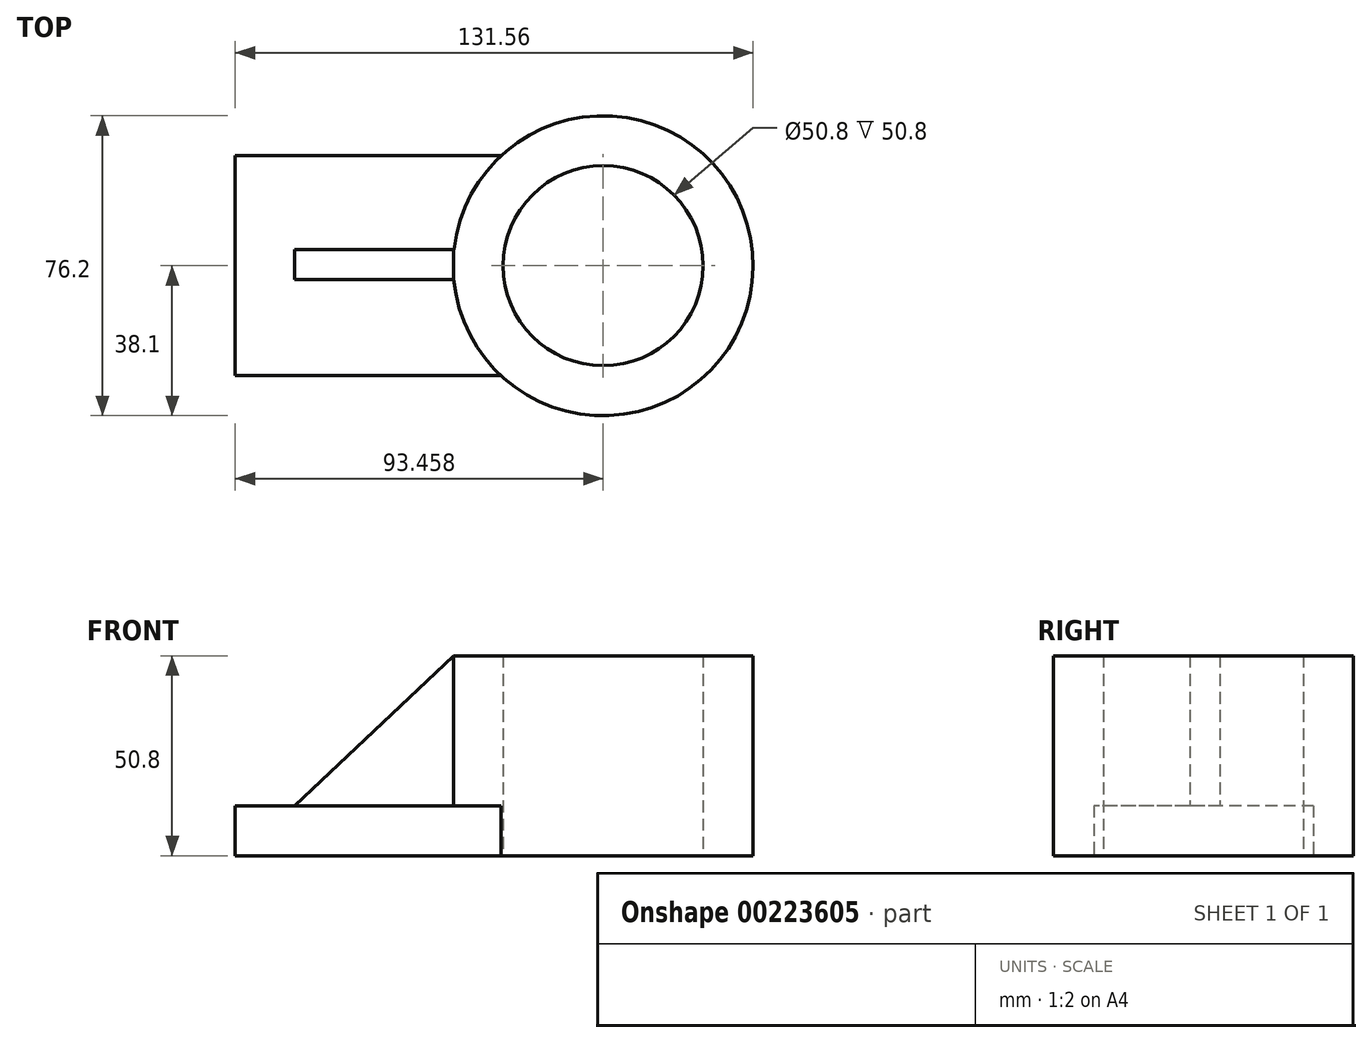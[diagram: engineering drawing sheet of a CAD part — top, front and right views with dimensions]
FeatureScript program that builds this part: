
annotation { "Feature Type Name" : "Feature", "Feature Type Description" : "" }
export const myFeature = defineFeature(function(context is Context, id is Id, definition is map)
    precondition{}
    {
        {
            var Q0;
            Q0=qCreatedBy(makeId("Top.planeOp"),FACE);
            var sketch = newSketch(context, id + "F0", { "sketchPlane" : qUnion([Q0])});
            skCircle(sketch, "E0", {"center": v(38.03, 0) * mm, "radius": 38.1 * mm});
            skCircle(sketch, "E1", {"center": v(38.03, 0) * mm, "radius": 25.4 * mm});
            skSolve(sketch);
        }
        {
            var Q0;
            Q0=makeQuery(id+"F0.imprint","IMPRINT",FACE,{"disambiguationData":[TD([[makeQuery(id+"F0.imprint","IMPRINT",EDGE,{"derivedFrom":sQuery(id+"F0.wireOp",EDGE,"E0")}),1.0]])]});
            extrude(context, id + "F1", {"entities" : qUnion([Q0]), "depth" : 50.8 * mm});
        }
        {
            var Q0;
            Q0=qCreatedBy(makeId("Top.planeOp"),FACE);
            var sketch = newSketch(context, id + "F2", { "sketchPlane" : qUnion([Q0])});
            skLineSegment(sketch, "E2.bottom", {"start": v(12.24, 27.93) * mm, "end": v(-55.43, 27.93) * mm});
            skLineSegment(sketch, "E2.top", {"start": v(12.24, -27.87) * mm, "end": v(-55.43, -27.87) * mm});
            skLineSegment(sketch, "E2.left", {"start": v(12.24, 27.93) * mm, "end": v(12.24, -27.87) * mm});
            skLineSegment(sketch, "E2.right", {"start": v(-55.43, 27.93) * mm, "end": v(-55.43, -27.87) * mm});
            skSolve(sketch);
        }
        {
            var Q0;
            Q0=makeQuery(id+"F2.imprint","IMPRINT",FACE,{"disambiguationData":[TD([[makeQuery(id+"F2.imprint","IMPRINT",EDGE,{"derivedFrom":sQuery(id+"F2.wireOp",EDGE,"E2.bottom")}),1.0]])]});
            extrude(context, id + "F3", {"entities" : qUnion([Q0]), "operationType" : NewBodyOperationType.ADD, "depth" : 12.7 * mm});
        }
        {
            var Q0;
            Q0=makeQuery(id+"F3.opExtrude","CAP_FACE",FACE,{"disambiguationData":[OSD([sQuery(id+"F2.wireOp",EDGE,"E2.bottom"),sQuery(id+"F2.wireOp",EDGE,"E2.top"),sQuery(id+"F2.wireOp",EDGE,"E2.left"),sQuery(id+"F2.wireOp",EDGE,"E2.right")])],"isStart":false});
            var sketch = newSketch(context, id + "F4", { "sketchPlane" : qUnion([Q0])});
            skLineSegment(sketch, "E3.bottom", {"start": v(0.16, 4.17) * mm, "end": v(-40.37, 4.17) * mm});
            skLineSegment(sketch, "E3.top", {"start": v(0.16, -3.45) * mm, "end": v(-40.37, -3.45) * mm});
            skLineSegment(sketch, "E3.left", {"start": v(0.16, 4.17) * mm, "end": v(0.16, -3.45) * mm});
            skLineSegment(sketch, "E3.right", {"start": v(-40.37, 4.17) * mm, "end": v(-40.37, -3.45) * mm});
            skSolve(sketch);
        }
        {
            var Q0;
            {var subQ0=sQuery(id+"F4.wireOp",EDGE,"E3.bottom");Q0=makeQuery(id+"F4.imprint","IMPRINT",FACE,{"disambiguationData":[TD([[makeQuery(id+"F4.imprint","IMPRINT",EDGE,{"derivedFrom":subQ0}),1.0]])]});}
            extrude(context, id + "F5", {"entities" : qUnion([Q0]), "operationType" : NewBodyOperationType.ADD, "depth" : 38.1 * mm});
        }
        {
            var Q0;
            Q0=makeQuery(id+"F5.opExtrude","SWEPT_FACE",FACE,{"disambiguationData":[OSD([sQuery(id+"F4.wireOp",EDGE,"E3.top")])]});
            var sketch = newSketch(context, id + "F6", { "sketchPlane" : qUnion([Q0])});
            skLineSegment(sketch, "E4", {"start": v(0.08, 50.8) * mm, "end": v(-40.37, 12.7) * mm});
            skLineSegment(sketch, "E5", {"start": v(-40.37, 12.7) * mm, "end": v(-40.37, 50.8) * mm});
            skLineSegment(sketch, "E6", {"start": v(-40.37, 50.8) * mm, "end": v(0.08, 50.8) * mm});
            skSolve(sketch);
        }
        {
            var Q0;
            Q0=makeQuery(id+"F6.imprint","IMPRINT",FACE,{"disambiguationData":[TD([[makeQuery(id+"F6.imprint","IMPRINT",EDGE,{"derivedFrom":sQuery(id+"F6.wireOp",EDGE,"E4")}),-1.0]])]});
            extrude(context, id + "F7", {"entities" : qUnion([Q0]), "operationType" : NewBodyOperationType.REMOVE, "oppositeDirection" : true, "depth" : 25.4 * mm});
        }
    });
